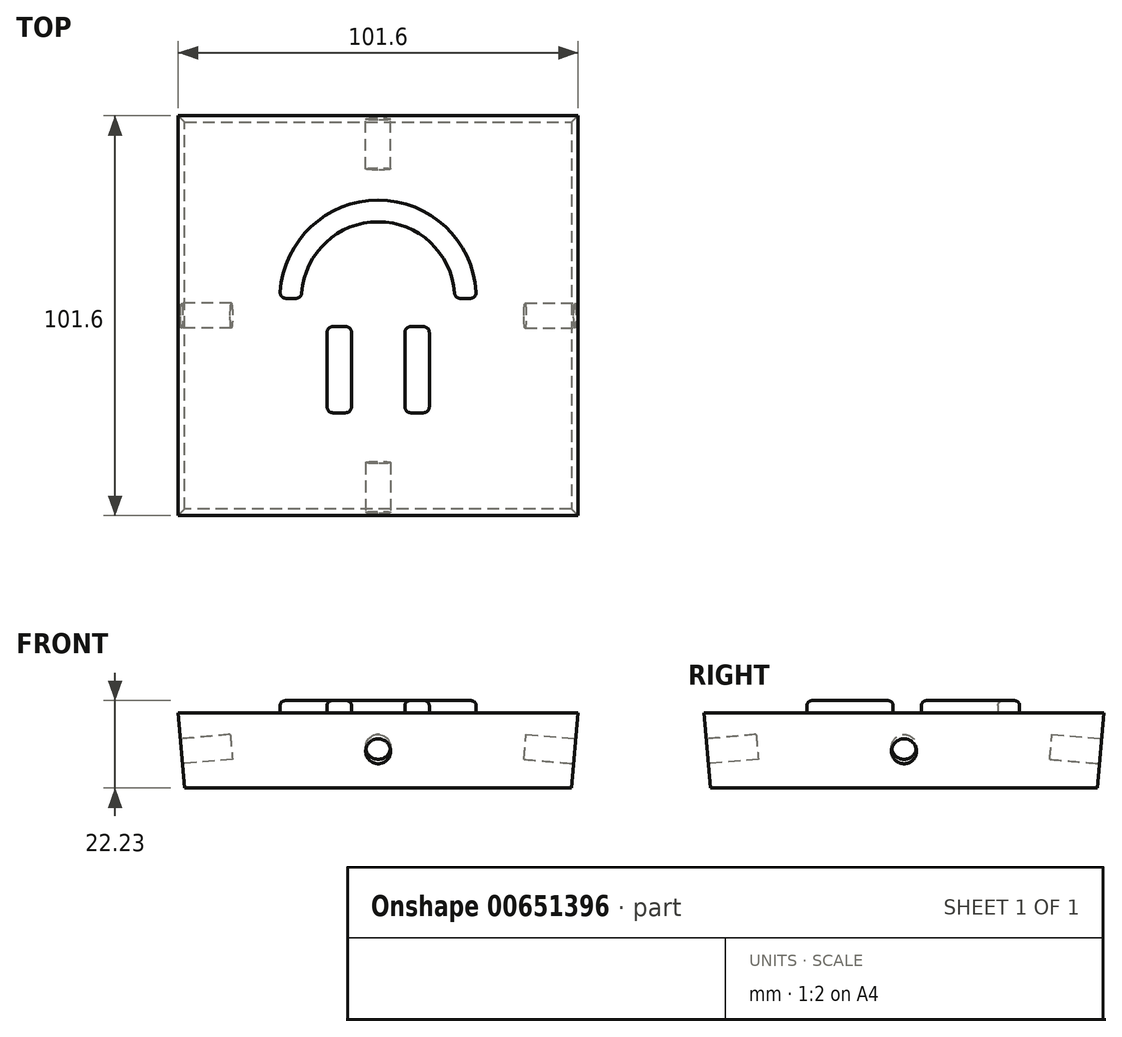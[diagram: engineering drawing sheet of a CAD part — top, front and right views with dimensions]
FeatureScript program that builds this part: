
annotation { "Feature Type Name" : "Feature", "Feature Type Description" : "" }
export const myFeature = defineFeature(function(context is Context, id is Id, definition is map)
    precondition{}
    {
        {
            var Q0;
            Q0=qCreatedBy(makeId("Top.planeOp"),FACE);
            var sketch = newSketch(context, id + "F0", { "sketchPlane" : qUnion([Q0])});
            skLineSegment(sketch, "E0.bottom", {"start": v(-50.8, 50.8) * mm, "end": v(50.8, 50.8) * mm});
            skLineSegment(sketch, "E0.top", {"start": v(-50.8, -50.8) * mm, "end": v(50.8, -50.8) * mm});
            skLineSegment(sketch, "E0.left", {"start": v(-50.8, 50.8) * mm, "end": v(-50.8, -50.8) * mm});
            skLineSegment(sketch, "E0.right", {"start": v(50.8, 50.8) * mm, "end": v(50.8, -50.8) * mm});
            skPoint(sketch, "E0.middle", {"position": v(0, 0) * mm});
            skSolve(sketch);
        }
        {
            var Q0;
            Q0=makeQuery(id+"F0.imprint","IMPRINT",FACE,{"disambiguationData":[TD([[makeQuery(id+"F0.imprint","IMPRINT",EDGE,{"derivedFrom":sQuery(id+"F0.wireOp",EDGE,"E0.bottom")}),-1.0]])]});
            extrude(context, id + "F1", {"entities" : qUnion([Q0]), "depth" : 19.05 * mm, "offsetDistance" : 25.4 * mm});
        }
        {
            var Q0;
            Q0=makeQuery(id+"F1.opExtrude","CAP_EDGE",EDGE,{"disambiguationData":[OSD([sQuery(id+"F0.wireOp",EDGE,"E0.right")])],"isStart":false});
            var Q1;
            Q1=makeQuery(id+"F1.opExtrude","CAP_EDGE",EDGE,{"disambiguationData":[OSD([sQuery(id+"F0.wireOp",EDGE,"E0.top")])],"isStart":false});
            var Q2;
            Q2=makeQuery(id+"F1.opExtrude","CAP_EDGE",EDGE,{"disambiguationData":[OSD([sQuery(id+"F0.wireOp",EDGE,"E0.left")])],"isStart":false});
            var Q3;
            Q3=makeQuery(id+"F1.opExtrude","CAP_EDGE",EDGE,{"disambiguationData":[OSD([sQuery(id+"F0.wireOp",EDGE,"E0.bottom")])],"isStart":false});
            chamfer(context, id + "F2", {"entities" : qUnion([Q0, Q1, Q2, Q3]), "chamferType" : ChamferType.OFFSET_ANGLE, "width" : 19.05 * mm, "oppositeDirection" : false, "angle" : 5 * degree, "tangentPropagation" : true});
        }
        {
            var Q0;
            Q0=makeQuery(id+"F2.opChamfer","BLEND_FACE",FACE,{"disambiguationData":[OSD([sQuery(id+"F0.wireOp",EDGE,"E0.bottom")])]});
            var sketch = newSketch(context, id + "F3", { "sketchPlane" : qUnion([Q0])});
            skLineSegment(sketch, "E1", {"start": v(-49.13, 14.7) * mm, "end": v(50.8, -4.43) * mm, "construction": true});
            skLineSegment(sketch, "E2", {"start": v(-50.8, -4.43) * mm, "end": v(49.13, 14.7) * mm, "construction": true});
            skCircle(sketch, "E3", {"center": v(0, 5.3) * mm, "radius": 3.18 * mm});
            skSolve(sketch);
        }
        {
            var Q0;
            Q0=makeQuery(id+"F3.imprint","IMPRINT",FACE,{"disambiguationData":[TD([[makeQuery(id+"F3.imprint","IMPRINT",EDGE,{"derivedFrom":sQuery(id+"F3.wireOp",EDGE,"E3")}),1.0]])]});
            extrude(context, id + "F4", {"entities" : qUnion([Q0]), "operationType" : NewBodyOperationType.REMOVE, "oppositeDirection" : true, "depth" : 12.7 * mm, "offsetDistance" : 25.4 * mm});
        }
        {
            var Q0;
            Q0=makeQuery(id+"F2.opChamfer","BLEND_FACE",FACE,{"disambiguationData":[OSD([sQuery(id+"F0.wireOp",EDGE,"E0.left")])]});
            var sketch = newSketch(context, id + "F5", { "sketchPlane" : qUnion([Q0])});
            skLineSegment(sketch, "E4", {"start": v(-49.13, 14.7) * mm, "end": v(50.8, -4.43) * mm, "construction": true});
            skLineSegment(sketch, "E5", {"start": v(-50.8, -4.43) * mm, "end": v(49.13, 14.7) * mm, "construction": true});
            skCircle(sketch, "E6", {"center": v(0, 5.3) * mm, "radius": 3.18 * mm});
            skSolve(sketch);
        }
        {
            var Q0;
            Q0=makeQuery(id+"F2.opChamfer","BLEND_FACE",FACE,{"disambiguationData":[OSD([sQuery(id+"F0.wireOp",EDGE,"E0.top")])]});
            var sketch = newSketch(context, id + "F6", { "sketchPlane" : qUnion([Q0])});
            skLineSegment(sketch, "E7", {"start": v(-49.13, 14.7) * mm, "end": v(50.8, -4.43) * mm, "construction": true});
            skLineSegment(sketch, "E8", {"start": v(-50.8, -4.43) * mm, "end": v(49.13, 14.7) * mm, "construction": true});
            skCircle(sketch, "E9", {"center": v(0, 5.3) * mm, "radius": 3.18 * mm});
            skSolve(sketch);
        }
        {
            var Q0;
            Q0=makeQuery(id+"F2.opChamfer","BLEND_FACE",FACE,{"disambiguationData":[OSD([sQuery(id+"F0.wireOp",EDGE,"E0.right")])]});
            var sketch = newSketch(context, id + "F7", { "sketchPlane" : qUnion([Q0])});
            skLineSegment(sketch, "E10", {"start": v(-49.13, 14.7) * mm, "end": v(50.8, -4.43) * mm, "construction": true});
            skLineSegment(sketch, "E11", {"start": v(-50.8, -4.43) * mm, "end": v(49.13, 14.7) * mm, "construction": true});
            skCircle(sketch, "E12", {"center": v(0, 5.3) * mm, "radius": 3.18 * mm});
            skSolve(sketch);
        }
        {
            var Q0;
            Q0=makeQuery(id+"F7.imprint","IMPRINT",FACE,{"disambiguationData":[TD([[makeQuery(id+"F7.imprint","IMPRINT",EDGE,{"derivedFrom":sQuery(id+"F7.wireOp",EDGE,"E12")}),1.0]])]});
            extrude(context, id + "F8", {"entities" : qUnion([Q0]), "operationType" : NewBodyOperationType.REMOVE, "oppositeDirection" : true, "depth" : 12.7 * mm, "offsetDistance" : 25.4 * mm});
        }
        {
            var Q0;
            Q0=makeQuery(id+"F6.imprint","IMPRINT",FACE,{"disambiguationData":[TD([[makeQuery(id+"F6.imprint","IMPRINT",EDGE,{"derivedFrom":sQuery(id+"F6.wireOp",EDGE,"E9")}),1.0]])]});
            extrude(context, id + "F9", {"entities" : qUnion([Q0]), "operationType" : NewBodyOperationType.REMOVE, "oppositeDirection" : true, "depth" : 12.7 * mm, "offsetDistance" : 25.4 * mm});
        }
        {
            var Q0;
            Q0=makeQuery(id+"F5.imprint","IMPRINT",FACE,{"disambiguationData":[TD([[makeQuery(id+"F5.imprint","IMPRINT",EDGE,{"derivedFrom":sQuery(id+"F5.wireOp",EDGE,"E6")}),1.0]])]});
            extrude(context, id + "F10", {"entities" : qUnion([Q0]), "operationType" : NewBodyOperationType.REMOVE, "oppositeDirection" : true, "depth" : 12.7 * mm, "offsetDistance" : 25.4 * mm});
        }
        {
            var Q0;
            Q0=makeQuery(id+"F1.opExtrude","CAP_FACE",FACE,{"disambiguationData":[OSD([sQuery(id+"F0.wireOp",EDGE,"E0.bottom"),sQuery(id+"F0.wireOp",EDGE,"E0.top"),sQuery(id+"F0.wireOp",EDGE,"E0.left"),sQuery(id+"F0.wireOp",EDGE,"E0.right")])],"isStart":true});
            var sketch = newSketch(context, id + "F11", { "sketchPlane" : qUnion([Q0])});
            skLineSegment(sketch, "E13.bottom", {"start": v(-11.51, 24.67) * mm, "end": v(-8.25, 24.67) * mm});
            skLineSegment(sketch, "E13.top", {"start": v(-11.51, 2.78) * mm, "end": v(-8.25, 2.78) * mm});
            skLineSegment(sketch, "E13.left", {"start": v(-12.99, 23.2) * mm, "end": v(-12.99, 4.25) * mm});
            skLineSegment(sketch, "E13.right", {"start": v(-6.78, 23.2) * mm, "end": v(-6.78, 4.25) * mm});
            skLineSegment(sketch, "E14", {"start": v(0, 0) * mm, "end": v(0, 24.5) * mm, "construction": true});
            skLineSegment(sketch, "E15.MirrorCS", {"start": v(11.51, 24.67) * mm, "end": v(8.25, 24.67) * mm});
            skLineSegment(sketch, "E16.MirrorCS", {"start": v(11.51, 2.78) * mm, "end": v(8.25, 2.78) * mm});
            skLineSegment(sketch, "E17.MirrorCS", {"start": v(6.78, 23.2) * mm, "end": v(6.78, 4.25) * mm});
            skLineSegment(sketch, "E18.MirrorCS", {"start": v(12.99, 23.2) * mm, "end": v(12.99, 4.25) * mm});
            skArc(sketch, "E19", {"start": v(-19.4, -5.78) * mm, "mid": v(0, -23.86) * mm, "end": v(19.4, -5.78) * mm});
            skArc(sketch, "E20", {"start": v(-24.9, -5.97) * mm, "mid": v(0, -29.36) * mm, "end": v(24.9, -5.97) * mm});
            skLineSegment(sketch, "E21", {"start": v(-23.43, -4.4) * mm, "end": v(-20.87, -4.4) * mm});
            skLineSegment(sketch, "E22.trimOffspring", {"start": v(20.87, -4.4) * mm, "end": v(23.43, -4.4) * mm});
            skPoint(sketch, "E23.visualSharp", {"position": v(-24.95, -4.4) * mm});
            skArc(sketch, "E23.filletArc", {"start": v(-23.43, -4.4) * mm, "mid": v(-24.5, -4.87) * mm, "end": v(-24.9, -5.97) * mm});
            skPoint(sketch, "E24.visualSharp", {"position": v(19.45, -4.4) * mm});
            skArc(sketch, "E24.filletArc", {"start": v(20.87, -4.4) * mm, "mid": v(19.86, -4.8) * mm, "end": v(19.4, -5.78) * mm});
            skPoint(sketch, "E25.visualSharp", {"position": v(-19.45, -4.4) * mm});
            skArc(sketch, "E25.filletArc", {"start": v(-19.4, -5.78) * mm, "mid": v(-19.86, -4.8) * mm, "end": v(-20.87, -4.4) * mm});
            skPoint(sketch, "E26.visualSharp", {"position": v(24.95, -4.4) * mm});
            skArc(sketch, "E26.filletArc", {"start": v(24.9, -5.97) * mm, "mid": v(24.5, -4.87) * mm, "end": v(23.43, -4.4) * mm});
            skPoint(sketch, "E27.visualSharp", {"position": v(6.78, 24.67) * mm});
            skArc(sketch, "E27.filletArc", {"start": v(8.25, 24.67) * mm, "mid": v(7.21, 24.24) * mm, "end": v(6.78, 23.2) * mm});
            skPoint(sketch, "E28.visualSharp", {"position": v(12.99, 24.67) * mm});
            skArc(sketch, "E28.filletArc", {"start": v(12.99, 23.2) * mm, "mid": v(12.56, 24.24) * mm, "end": v(11.51, 24.67) * mm});
            skPoint(sketch, "E29.visualSharp", {"position": v(6.78, 2.78) * mm});
            skArc(sketch, "E29.filletArc", {"start": v(6.78, 4.25) * mm, "mid": v(7.21, 3.2) * mm, "end": v(8.25, 2.78) * mm});
            skPoint(sketch, "E30.visualSharp", {"position": v(12.99, 2.78) * mm});
            skArc(sketch, "E30.filletArc", {"start": v(11.51, 2.78) * mm, "mid": v(12.56, 3.2) * mm, "end": v(12.99, 4.25) * mm});
            skPoint(sketch, "E31.visualSharp", {"position": v(-12.99, 24.67) * mm});
            skArc(sketch, "E31.filletArc", {"start": v(-11.51, 24.67) * mm, "mid": v(-12.56, 24.24) * mm, "end": v(-12.99, 23.2) * mm});
            skPoint(sketch, "E32.visualSharp", {"position": v(-6.78, 24.67) * mm});
            skArc(sketch, "E32.filletArc", {"start": v(-6.78, 23.2) * mm, "mid": v(-7.21, 24.24) * mm, "end": v(-8.25, 24.67) * mm});
            skPoint(sketch, "E33.visualSharp", {"position": v(-12.99, 2.78) * mm});
            skArc(sketch, "E33.filletArc", {"start": v(-12.99, 4.25) * mm, "mid": v(-12.56, 3.2) * mm, "end": v(-11.51, 2.78) * mm});
            skPoint(sketch, "E34.visualSharp", {"position": v(-6.78, 2.78) * mm});
            skArc(sketch, "E34.filletArc", {"start": v(-8.25, 2.78) * mm, "mid": v(-7.21, 3.2) * mm, "end": v(-6.78, 4.25) * mm});
            skSolve(sketch);
        }
        {
            var Q0;
            Q0=qSketchRegion(id+"F11",true);
            extrude(context, id + "F12", {"entities" : qUnion([Q0]), "operationType" : NewBodyOperationType.ADD, "depth" : 3.17 * mm, "offsetDistance" : 25.4 * mm});
        }
        {
            var Q0;
            Q0=makeQuery(id+"F12.opExtrude","CAP_EDGE",EDGE,{"disambiguationData":[OSD([sQuery(id+"F11.wireOp",EDGE,"E20")])],"isStart":false});
            var Q1;
            Q1=makeQuery(id+"F12.opExtrude","CAP_EDGE",EDGE,{"disambiguationData":[OSD([sQuery(id+"F11.wireOp",EDGE,"E19")])],"isStart":false});
            var Q2;
            Q2=makeQuery(id+"F12.opExtrude","CAP_EDGE",EDGE,{"disambiguationData":[OSD([sQuery(id+"F11.wireOp",EDGE,"E21")])],"isStart":false});
            var Q3;
            Q3=makeQuery(id+"F12.opExtrude","CAP_EDGE",EDGE,{"disambiguationData":[OSD([sQuery(id+"F11.wireOp",EDGE,"E25.filletArc")])],"isStart":false});
            var Q4;
            Q4=makeQuery(id+"F12.opExtrude","CAP_EDGE",EDGE,{"disambiguationData":[OSD([sQuery(id+"F11.wireOp",EDGE,"E23.filletArc")])],"isStart":false});
            var Q5;
            Q5=makeQuery(id+"F12.opExtrude","CAP_EDGE",EDGE,{"disambiguationData":[OSD([sQuery(id+"F11.wireOp",EDGE,"E24.filletArc")])],"isStart":false});
            var Q6;
            Q6=makeQuery(id+"F12.opExtrude","CAP_EDGE",EDGE,{"disambiguationData":[OSD([sQuery(id+"F11.wireOp",EDGE,"E22.trimOffspring")])],"isStart":false});
            var Q7;
            Q7=makeQuery(id+"F12.opExtrude","CAP_EDGE",EDGE,{"disambiguationData":[OSD([sQuery(id+"F11.wireOp",EDGE,"E26.filletArc")])],"isStart":false});
            var Q8;
            Q8=makeQuery(id+"F12.opExtrude","CAP_EDGE",EDGE,{"disambiguationData":[OSD([sQuery(id+"F11.wireOp",EDGE,"E15.MirrorCS")])],"isStart":false});
            var Q9;
            Q9=makeQuery(id+"F12.opExtrude","CAP_EDGE",EDGE,{"disambiguationData":[OSD([sQuery(id+"F11.wireOp",EDGE,"E27.filletArc")])],"isStart":false});
            var Q10;
            Q10=makeQuery(id+"F12.opExtrude","CAP_EDGE",EDGE,{"disambiguationData":[OSD([sQuery(id+"F11.wireOp",EDGE,"E17.MirrorCS")])],"isStart":false});
            var Q11;
            Q11=makeQuery(id+"F12.opExtrude","CAP_EDGE",EDGE,{"disambiguationData":[OSD([sQuery(id+"F11.wireOp",EDGE,"E29.filletArc")])],"isStart":false});
            var Q12;
            Q12=makeQuery(id+"F12.opExtrude","CAP_EDGE",EDGE,{"disambiguationData":[OSD([sQuery(id+"F11.wireOp",EDGE,"E16.MirrorCS")])],"isStart":false});
            var Q13;
            Q13=makeQuery(id+"F12.opExtrude","CAP_EDGE",EDGE,{"disambiguationData":[OSD([sQuery(id+"F11.wireOp",EDGE,"E30.filletArc")])],"isStart":false});
            var Q14;
            Q14=makeQuery(id+"F12.opExtrude","CAP_EDGE",EDGE,{"disambiguationData":[OSD([sQuery(id+"F11.wireOp",EDGE,"E28.filletArc")])],"isStart":false});
            var Q15;
            Q15=makeQuery(id+"F12.opExtrude","CAP_EDGE",EDGE,{"disambiguationData":[OSD([sQuery(id+"F11.wireOp",EDGE,"E18.MirrorCS")])],"isStart":false});
            var Q16;
            Q16=makeQuery(id+"F12.opExtrude","CAP_EDGE",EDGE,{"disambiguationData":[OSD([sQuery(id+"F11.wireOp",EDGE,"E13.right")])],"isStart":false});
            var Q17;
            Q17=makeQuery(id+"F12.opExtrude","CAP_EDGE",EDGE,{"disambiguationData":[OSD([sQuery(id+"F11.wireOp",EDGE,"E32.filletArc")])],"isStart":false});
            var Q18;
            Q18=makeQuery(id+"F12.opExtrude","CAP_EDGE",EDGE,{"disambiguationData":[OSD([sQuery(id+"F11.wireOp",EDGE,"E13.bottom")])],"isStart":false});
            var Q19;
            Q19=makeQuery(id+"F12.opExtrude","CAP_EDGE",EDGE,{"disambiguationData":[OSD([sQuery(id+"F11.wireOp",EDGE,"E31.filletArc")])],"isStart":false});
            var Q20;
            Q20=makeQuery(id+"F12.opExtrude","CAP_EDGE",EDGE,{"disambiguationData":[OSD([sQuery(id+"F11.wireOp",EDGE,"E13.left")])],"isStart":false});
            var Q21;
            Q21=makeQuery(id+"F12.opExtrude","CAP_EDGE",EDGE,{"disambiguationData":[OSD([sQuery(id+"F11.wireOp",EDGE,"E33.filletArc")])],"isStart":false});
            var Q22;
            Q22=makeQuery(id+"F12.opExtrude","CAP_EDGE",EDGE,{"disambiguationData":[OSD([sQuery(id+"F11.wireOp",EDGE,"E13.top")])],"isStart":false});
            var Q23;
            Q23=makeQuery(id+"F12.opExtrude","CAP_EDGE",EDGE,{"disambiguationData":[OSD([sQuery(id+"F11.wireOp",EDGE,"E34.filletArc")])],"isStart":false});
            fillet(context, id + "F13", {"entities" : qUnion([Q0, Q1, Q2, Q3, Q4, Q5, Q6, Q7, Q8, Q9, Q10, Q11, Q12, Q13, Q14, Q15, Q16, Q17, Q18, Q19, Q20, Q21, Q22, Q23]), "radius" : 1.27 * mm, "tangentPropagation" : true, "allowEdgeOverflow" : false});
        }
        {
            var Q0;
            Q0=makeQuery(id+"F1.opExtrude","CAP_FACE",FACE,{"disambiguationData":[OSD([sQuery(id+"F0.wireOp",EDGE,"E0.bottom"),sQuery(id+"F0.wireOp",EDGE,"E0.top"),sQuery(id+"F0.wireOp",EDGE,"E0.left"),sQuery(id+"F0.wireOp",EDGE,"E0.right")])],"isStart":false});
            var sketch = newSketch(context, id + "F14", { "sketchPlane" : qUnion([Q0])});
            skLineSegment(sketch, "E35", {"start": v(55.15, 29.48) * mm, "end": v(55.15, -28.93) * mm, "construction": true});
            skSolve(sketch);
        }
        {
            var Q0;
            Q0=makeQuery(id+"F1.opExtrude","SWEPT_BODY",BODY,{"disambiguationData":[OSD([sQuery(id+"F0.wireOp",EDGE,"E0.bottom"),sQuery(id+"F0.wireOp",EDGE,"E0.top"),sQuery(id+"F0.wireOp",EDGE,"E0.left"),sQuery(id+"F0.wireOp",EDGE,"E0.right")])]});
            var Q1;
            Q1=sQuery(id+"F14.wireOp",EDGE,"E35");
            transform(context, id + "F15", {"entities" : qUnion([Q0]), "transformType" : TransformType.ROTATION, "transformAxis" : qUnion([Q1]), "angle" : 180 * degree, "makeCopy" : false});
        }
    });
